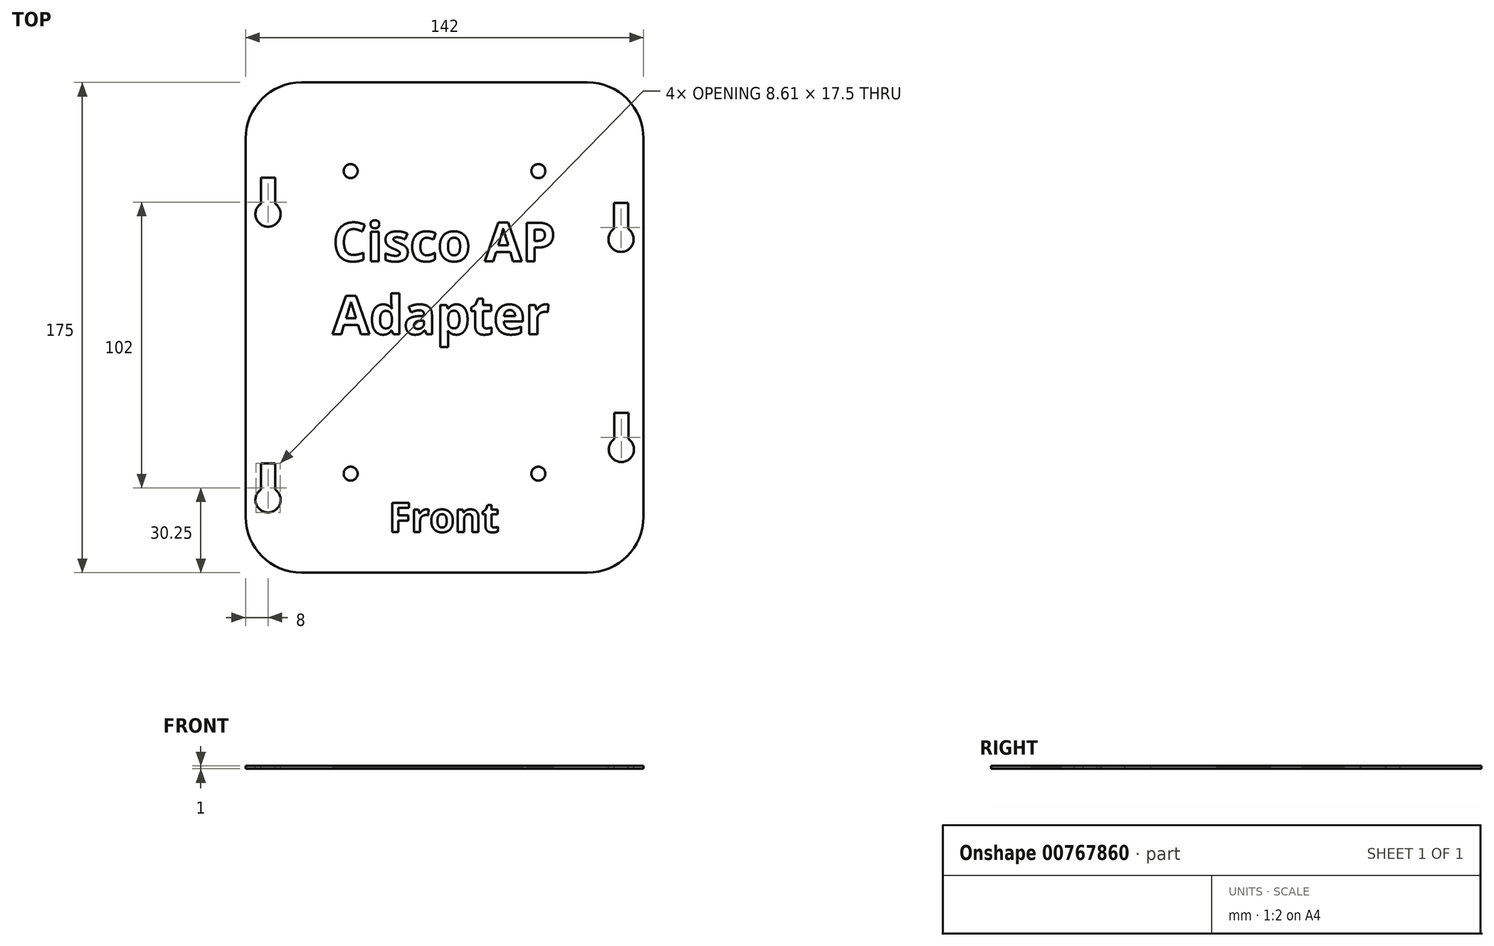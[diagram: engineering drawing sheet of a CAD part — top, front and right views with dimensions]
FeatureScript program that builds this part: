
annotation { "Feature Type Name" : "Feature", "Feature Type Description" : "" }
export const myFeature = defineFeature(function(context is Context, id is Id, definition is map)
    precondition{}
    {
        {
            var Q0;
            Q0=qCreatedBy(makeId("Top.planeOp"),FACE);
            var sketch = newSketch(context, id + "F0", { "sketchPlane" : qUnion([Q0])});
            skLineSegment(sketch, "E0.bottom", {"start": v(-51, 87.5) * mm, "end": v(51, 87.5) * mm});
            skLineSegment(sketch, "E0.top", {"start": v(-51, -87.5) * mm, "end": v(51, -87.5) * mm});
            skLineSegment(sketch, "E0.left", {"start": v(-71, 67.5) * mm, "end": v(-71, -67.5) * mm});
            skLineSegment(sketch, "E0.right", {"start": v(71, 67.5) * mm, "end": v(71, -67.5) * mm});
            skPoint(sketch, "E0.middle", {"position": v(0, 0) * mm});
            skPoint(sketch, "E1.visualSharp", {"position": v(-71, 87.5) * mm});
            skArc(sketch, "E1.filletArc", {"start": v(-51, 87.5) * mm, "mid": v(-65.14, 81.64) * mm, "end": v(-71, 67.5) * mm});
            skPoint(sketch, "E2.visualSharp", {"position": v(71, 87.5) * mm});
            skArc(sketch, "E2.filletArc", {"start": v(71, 67.5) * mm, "mid": v(65.14, 81.64) * mm, "end": v(51, 87.5) * mm});
            skPoint(sketch, "E3.visualSharp", {"position": v(-71, -87.5) * mm});
            skArc(sketch, "E3.filletArc", {"start": v(-71, -67.5) * mm, "mid": v(-65.14, -81.64) * mm, "end": v(-51, -87.5) * mm});
            skPoint(sketch, "E4.visualSharp", {"position": v(71, -87.5) * mm});
            skArc(sketch, "E4.filletArc", {"start": v(51, -87.5) * mm, "mid": v(65.14, -81.64) * mm, "end": v(71, -67.5) * mm});
            skLineSegment(sketch, "E5.top", {"start": v(-60.5, 53.5) * mm, "end": v(-65.5, 53.5) * mm});
            skLineSegment(sketch, "E5.left", {"start": v(-60.5, 44.24) * mm, "end": v(-60.5, 53.5) * mm});
            skLineSegment(sketch, "E5.right", {"start": v(-65.5, 44.24) * mm, "end": v(-65.5, 53.5) * mm});
            skArc(sketch, "E6", {"start": v(-65.5, 44.24) * mm, "mid": v(-63, 36) * mm, "end": v(-60.5, 44.24) * mm});
            skLineSegment(sketch, "E7.top", {"start": v(65.5, 44.5) * mm, "end": v(60.5, 44.5) * mm});
            skLineSegment(sketch, "E7.left", {"start": v(65.5, 35.24) * mm, "end": v(65.5, 44.5) * mm});
            skLineSegment(sketch, "E7.right", {"start": v(60.5, 35.24) * mm, "end": v(60.5, 44.5) * mm});
            skArc(sketch, "E8", {"start": v(60.5, 35.24) * mm, "mid": v(63, 27) * mm, "end": v(65.5, 35.24) * mm});
            skLineSegment(sketch, "E9.top", {"start": v(65.62, -30.5) * mm, "end": v(60.62, -30.5) * mm});
            skLineSegment(sketch, "E9.left", {"start": v(65.62, -39.76) * mm, "end": v(65.62, -30.5) * mm});
            skLineSegment(sketch, "E9.right", {"start": v(60.62, -39.76) * mm, "end": v(60.62, -30.5) * mm});
            skArc(sketch, "E10", {"start": v(60.62, -39.76) * mm, "mid": v(63.12, -48) * mm, "end": v(65.62, -39.76) * mm});
            skLineSegment(sketch, "E11.top", {"start": v(-60.5, -48.5) * mm, "end": v(-65.5, -48.5) * mm});
            skLineSegment(sketch, "E11.left", {"start": v(-60.5, -57.76) * mm, "end": v(-60.5, -48.5) * mm});
            skLineSegment(sketch, "E11.right", {"start": v(-65.5, -57.76) * mm, "end": v(-65.5, -48.5) * mm});
            skArc(sketch, "E12", {"start": v(-65.5, -57.76) * mm, "mid": v(-63, -66) * mm, "end": v(-60.5, -57.76) * mm});
            skCircle(sketch, "E13", {"center": v(-33.5, 55.84) * mm, "radius": 2.5 * mm});
            skCircle(sketch, "E14", {"center": v(33.5, 55.84) * mm, "radius": 2.5 * mm});
            skCircle(sketch, "E15", {"center": v(33.5, -52.16) * mm, "radius": 2.5 * mm});
            skCircle(sketch, "E16", {"center": v(-33.5, -52.16) * mm, "radius": 2.5 * mm});
            skText(sketch, "E17", { "text": "Cisco AP\nAdapter", "fontName": "OpenSans-Bold.ttf"});
            skText(sketch, "E18", { "text": "Front", "fontName": "OpenSans-Bold.ttf"});
            const initialGuessF0  = {"E17": [-0.04, 0.02369, 1, 0, 0.01381], "E18": [-0.02, -0.07299, 1, 0, 0.01049]};
            skSetInitialGuess(sketch, initialGuessF0);
            skSolve(sketch);
        }
        {
            var Q0;
            Q0=makeQuery(id+"F0.imprint","IMPRINT",FACE,{"disambiguationData":[TD([[makeQuery(id+"F0.imprint","IMPRINT",EDGE,{"derivedFrom":sQuery(id+"F0.wireOp",EDGE,"E0.bottom")}),-1.0]])]});
            var Q1;
            Q1=makeQuery(id+"F0.imprint","IMPRINT",FACE,{"disambiguationData":[TD([[makeQuery(id+"F0.imprint","IMPRINT",EDGE,{"derivedFrom":sQuery(id+"F0.wireOp",EDGE,"E17.sketch_text.stroke-0")}),-1.0]])]});
            var Q2;
            Q2=makeQuery(id+"F0.imprint","IMPRINT",FACE,{"disambiguationData":[TD([[makeQuery(id+"F0.imprint","IMPRINT",EDGE,{"derivedFrom":sQuery(id+"F0.wireOp",EDGE,"E17.sketch_text.stroke-20")}),-1.0]])]});
            var Q3;
            Q3=makeQuery(id+"F0.imprint","IMPRINT",FACE,{"disambiguationData":[TD([[makeQuery(id+"F0.imprint","IMPRINT",EDGE,{"derivedFrom":sQuery(id+"F0.wireOp",EDGE,"E17.sketch_text.stroke-15")}),-1.0]])]});
            var Q4;
            Q4=makeQuery(id+"F0.imprint","IMPRINT",FACE,{"disambiguationData":[TD([[makeQuery(id+"F0.imprint","IMPRINT",EDGE,{"derivedFrom":sQuery(id+"F0.wireOp",EDGE,"E17.sketch_text.stroke-24")}),-1.0]])]});
            var Q5;
            Q5=makeQuery(id+"F0.imprint","IMPRINT",FACE,{"disambiguationData":[TD([[makeQuery(id+"F0.imprint","IMPRINT",EDGE,{"derivedFrom":sQuery(id+"F0.wireOp",EDGE,"E17.sketch_text.stroke-50")}),-1.0]])]});
            var Q6;
            Q6=makeQuery(id+"F0.imprint","IMPRINT",FACE,{"disambiguationData":[TD([[makeQuery(id+"F0.imprint","IMPRINT",EDGE,{"derivedFrom":sQuery(id+"F0.wireOp",EDGE,"E17.sketch_text.stroke-64")}),-1.0]])]});
            var Q7;
            Q7=makeQuery(id+"F0.imprint","IMPRINT",FACE,{"disambiguationData":[TD([[makeQuery(id+"F0.imprint","IMPRINT",EDGE,{"derivedFrom":sQuery(id+"F0.wireOp",EDGE,"E17.sketch_text.stroke-64")}),1.0]])]});
            var Q8;
            Q8=makeQuery(id+"F0.imprint","IMPRINT",FACE,{"disambiguationData":[TD([[makeQuery(id+"F0.imprint","IMPRINT",EDGE,{"derivedFrom":sQuery(id+"F0.wireOp",EDGE,"E17.sketch_text.stroke-82")}),-1.0]])]});
            var Q9;
            Q9=makeQuery(id+"F0.imprint","IMPRINT",FACE,{"disambiguationData":[TD([[makeQuery(id+"F0.imprint","IMPRINT",EDGE,{"derivedFrom":sQuery(id+"F0.wireOp",EDGE,"E17.sketch_text.stroke-90")}),1.0]])]});
            var Q10;
            Q10=makeQuery(id+"F0.imprint","IMPRINT",FACE,{"disambiguationData":[TD([[makeQuery(id+"F0.imprint","IMPRINT",EDGE,{"derivedFrom":sQuery(id+"F0.wireOp",EDGE,"E17.sketch_text.stroke-94")}),-1.0]])]});
            var Q11;
            Q11=makeQuery(id+"F0.imprint","IMPRINT",FACE,{"disambiguationData":[TD([[makeQuery(id+"F0.imprint","IMPRINT",EDGE,{"derivedFrom":sQuery(id+"F0.wireOp",EDGE,"E17.sketch_text.stroke-94")}),1.0]])]});
            var Q12;
            Q12=makeQuery(id+"F0.imprint","IMPRINT",FACE,{"disambiguationData":[TD([[makeQuery(id+"F0.imprint","IMPRINT",EDGE,{"derivedFrom":sQuery(id+"F0.wireOp",EDGE,"E17.sketch_text.stroke-110")}),-1.0]])]});
            var Q13;
            Q13=makeQuery(id+"F0.imprint","IMPRINT",FACE,{"disambiguationData":[TD([[makeQuery(id+"F0.imprint","IMPRINT",EDGE,{"derivedFrom":sQuery(id+"F0.wireOp",EDGE,"E17.sketch_text.stroke-118")}),1.0]])]});
            var Q14;
            Q14=makeQuery(id+"F0.imprint","IMPRINT",FACE,{"disambiguationData":[TD([[makeQuery(id+"F0.imprint","IMPRINT",EDGE,{"derivedFrom":sQuery(id+"F0.wireOp",EDGE,"E17.sketch_text.stroke-122")}),-1.0]])]});
            var Q15;
            Q15=makeQuery(id+"F0.imprint","IMPRINT",FACE,{"disambiguationData":[TD([[makeQuery(id+"F0.imprint","IMPRINT",EDGE,{"derivedFrom":sQuery(id+"F0.wireOp",EDGE,"E17.sketch_text.stroke-136")}),1.0]])]});
            var Q16;
            Q16=makeQuery(id+"F0.imprint","IMPRINT",FACE,{"disambiguationData":[TD([[makeQuery(id+"F0.imprint","IMPRINT",EDGE,{"derivedFrom":sQuery(id+"F0.wireOp",EDGE,"E17.sketch_text.stroke-145")}),-1.0]])]});
            var Q17;
            Q17=makeQuery(id+"F0.imprint","IMPRINT",FACE,{"disambiguationData":[TD([[makeQuery(id+"F0.imprint","IMPRINT",EDGE,{"derivedFrom":sQuery(id+"F0.wireOp",EDGE,"E17.sketch_text.stroke-163")}),1.0]])]});
            var Q18;
            Q18=makeQuery(id+"F0.imprint","IMPRINT",FACE,{"disambiguationData":[TD([[makeQuery(id+"F0.imprint","IMPRINT",EDGE,{"derivedFrom":sQuery(id+"F0.wireOp",EDGE,"E17.sketch_text.stroke-170")}),-1.0]])]});
            var Q19;
            Q19=makeQuery(id+"F0.imprint","IMPRINT",FACE,{"disambiguationData":[TD([[makeQuery(id+"F0.imprint","IMPRINT",EDGE,{"derivedFrom":sQuery(id+"F0.wireOp",EDGE,"E17.sketch_text.stroke-185")}),1.0]])]});
            var Q20;
            Q20=makeQuery(id+"F0.imprint","IMPRINT",FACE,{"disambiguationData":[TD([[makeQuery(id+"F0.imprint","IMPRINT",EDGE,{"derivedFrom":sQuery(id+"F0.wireOp",EDGE,"E17.sketch_text.stroke-193")}),-1.0]])]});
            var Q21;
            Q21=makeQuery(id+"F0.imprint","IMPRINT",FACE,{"disambiguationData":[TD([[makeQuery(id+"F0.imprint","IMPRINT",EDGE,{"derivedFrom":sQuery(id+"F0.wireOp",EDGE,"E17.sketch_text.stroke-211")}),-1.0]])]});
            var Q22;
            Q22=makeQuery(id+"F0.imprint","IMPRINT",FACE,{"disambiguationData":[TD([[makeQuery(id+"F0.imprint","IMPRINT",EDGE,{"derivedFrom":sQuery(id+"F0.wireOp",EDGE,"E17.sketch_text.stroke-211")}),1.0]])]});
            var Q23;
            Q23=makeQuery(id+"F0.imprint","IMPRINT",FACE,{"disambiguationData":[TD([[makeQuery(id+"F0.imprint","IMPRINT",EDGE,{"derivedFrom":sQuery(id+"F0.wireOp",EDGE,"E17.sketch_text.stroke-231")}),-1.0]])]});
            var Q24;
            Q24=makeQuery(id+"F0.imprint","IMPRINT",FACE,{"disambiguationData":[TD([[makeQuery(id+"F0.imprint","IMPRINT",EDGE,{"derivedFrom":sQuery(id+"F0.wireOp",EDGE,"E18.sketch_text.stroke-0")}),-1.0]])]});
            var Q25;
            Q25=makeQuery(id+"F0.imprint","IMPRINT",FACE,{"disambiguationData":[TD([[makeQuery(id+"F0.imprint","IMPRINT",EDGE,{"derivedFrom":sQuery(id+"F0.wireOp",EDGE,"E18.sketch_text.stroke-10")}),-1.0]])]});
            var Q26;
            Q26=makeQuery(id+"F0.imprint","IMPRINT",FACE,{"disambiguationData":[TD([[makeQuery(id+"F0.imprint","IMPRINT",EDGE,{"derivedFrom":sQuery(id+"F0.wireOp",EDGE,"E18.sketch_text.stroke-23")}),-1.0]])]});
            var Q27;
            Q27=makeQuery(id+"F0.imprint","IMPRINT",FACE,{"disambiguationData":[TD([[makeQuery(id+"F0.imprint","IMPRINT",EDGE,{"derivedFrom":sQuery(id+"F0.wireOp",EDGE,"E18.sketch_text.stroke-23")}),1.0]])]});
            var Q28;
            Q28=makeQuery(id+"F0.imprint","IMPRINT",FACE,{"disambiguationData":[TD([[makeQuery(id+"F0.imprint","IMPRINT",EDGE,{"derivedFrom":sQuery(id+"F0.wireOp",EDGE,"E18.sketch_text.stroke-41")}),-1.0]])]});
            var Q29;
            Q29=makeQuery(id+"F0.imprint","IMPRINT",FACE,{"disambiguationData":[TD([[makeQuery(id+"F0.imprint","IMPRINT",EDGE,{"derivedFrom":sQuery(id+"F0.wireOp",EDGE,"E18.sketch_text.stroke-58")}),-1.0]])]});
            extrude(context, id + "F1", {"entities" : qUnion([Q0, Q1, Q2, Q3, Q4, Q5, Q6, Q7, Q8, Q9, Q10, Q11, Q12, Q13, Q14, Q15, Q16, Q17, Q18, Q19, Q20, Q21, Q22, Q23, Q24, Q25, Q26, Q27, Q28, Q29]), "oppositeDirection" : true, "depth" : 0.5 * mm, "offsetDistance" : 25 * mm});
        }
        {
            var Q0;
            Q0 = qSketchRegion(id + "F0", true);
            var Q1;
            Q1=makeQuery(id+"F0.imprint","IMPRINT",FACE,{"disambiguationData":[TD([[makeQuery(id+"F0.imprint","IMPRINT",EDGE,{"derivedFrom":sQuery(id+"F0.wireOp",EDGE,"E17.sketch_text.stroke-64")}),1.0]])]});
            var Q2;
            Q2=makeQuery(id+"F0.imprint","IMPRINT",FACE,{"disambiguationData":[TD([[makeQuery(id+"F0.imprint","IMPRINT",EDGE,{"derivedFrom":sQuery(id+"F0.wireOp",EDGE,"E17.sketch_text.stroke-90")}),1.0]])]});
            var Q3;
            Q3=makeQuery(id+"F0.imprint","IMPRINT",FACE,{"disambiguationData":[TD([[makeQuery(id+"F0.imprint","IMPRINT",EDGE,{"derivedFrom":sQuery(id+"F0.wireOp",EDGE,"E17.sketch_text.stroke-94")}),1.0]])]});
            var Q4;
            Q4=makeQuery(id+"F0.imprint","IMPRINT",FACE,{"disambiguationData":[TD([[makeQuery(id+"F0.imprint","IMPRINT",EDGE,{"derivedFrom":sQuery(id+"F0.wireOp",EDGE,"E17.sketch_text.stroke-118")}),1.0]])]});
            var Q5;
            Q5=makeQuery(id+"F0.imprint","IMPRINT",FACE,{"disambiguationData":[TD([[makeQuery(id+"F0.imprint","IMPRINT",EDGE,{"derivedFrom":sQuery(id+"F0.wireOp",EDGE,"E17.sketch_text.stroke-136")}),1.0]])]});
            var Q6;
            Q6=makeQuery(id+"F0.imprint","IMPRINT",FACE,{"disambiguationData":[TD([[makeQuery(id+"F0.imprint","IMPRINT",EDGE,{"derivedFrom":sQuery(id+"F0.wireOp",EDGE,"E17.sketch_text.stroke-163")}),1.0]])]});
            var Q7;
            Q7=makeQuery(id+"F0.imprint","IMPRINT",FACE,{"disambiguationData":[TD([[makeQuery(id+"F0.imprint","IMPRINT",EDGE,{"derivedFrom":sQuery(id+"F0.wireOp",EDGE,"E17.sketch_text.stroke-185")}),1.0]])]});
            var Q8;
            Q8=makeQuery(id+"F0.imprint","IMPRINT",FACE,{"disambiguationData":[TD([[makeQuery(id+"F0.imprint","IMPRINT",EDGE,{"derivedFrom":sQuery(id+"F0.wireOp",EDGE,"E17.sketch_text.stroke-211")}),1.0]])]});
            var Q9;
            Q9=makeQuery(id+"F0.imprint","IMPRINT",FACE,{"disambiguationData":[TD([[makeQuery(id+"F0.imprint","IMPRINT",EDGE,{"derivedFrom":sQuery(id+"F0.wireOp",EDGE,"E18.sketch_text.stroke-23")}),1.0]])]});
            extrude(context, id + "F2", {"entities" : qUnion([Q0, Q1, Q2, Q3, Q4, Q5, Q6, Q7, Q8, Q9]), "operationType" : NewBodyOperationType.ADD, "depth" : 0.5 * mm, "offsetDistance" : 25 * mm});
        }
    });
